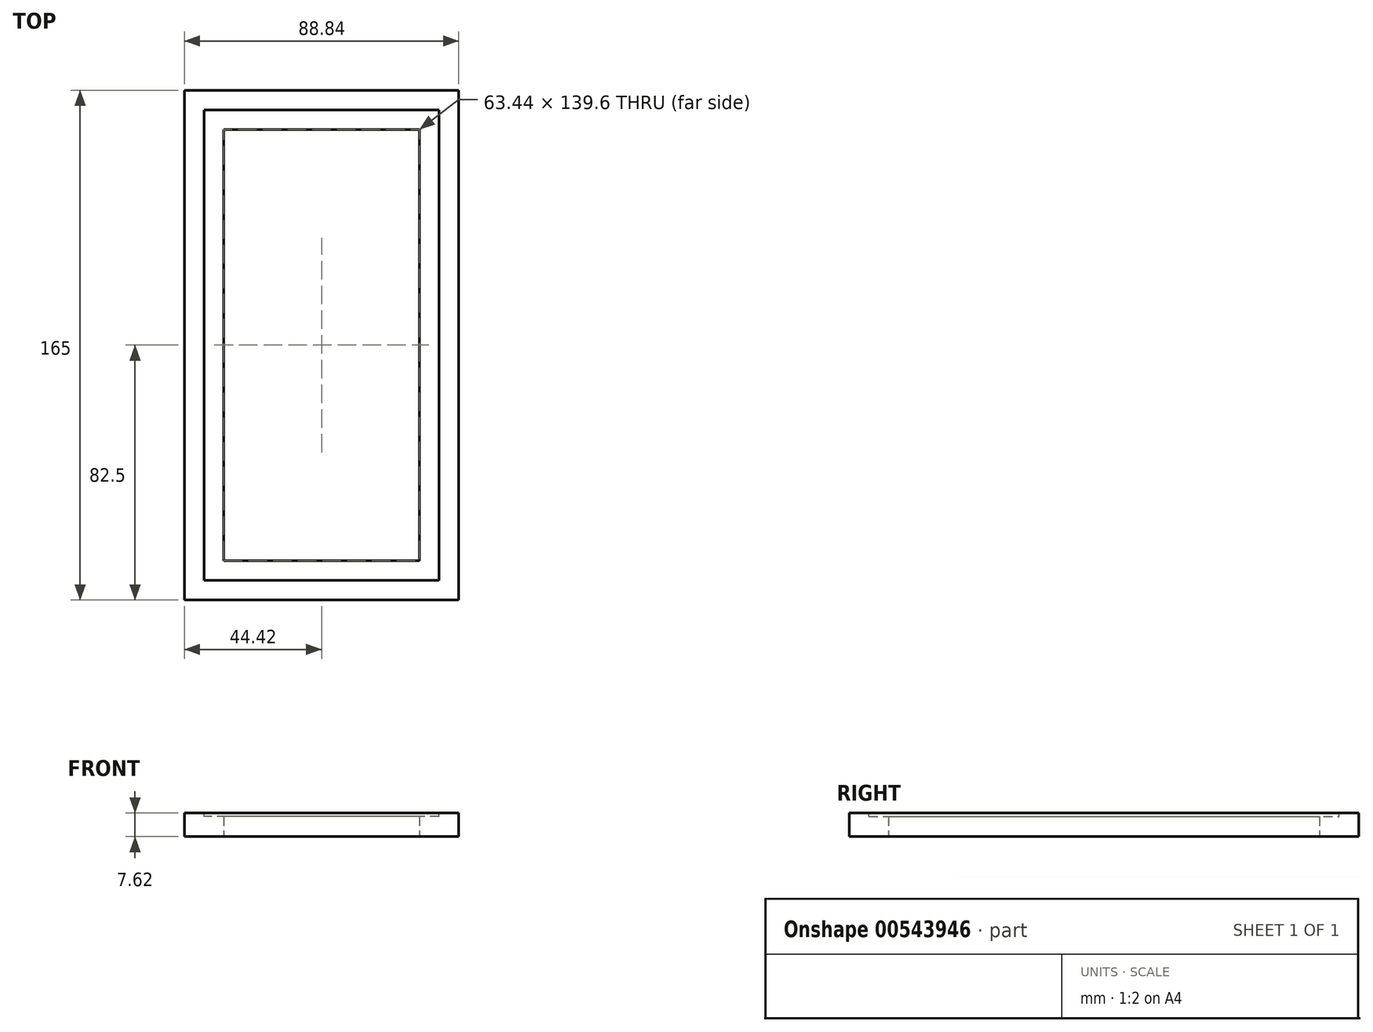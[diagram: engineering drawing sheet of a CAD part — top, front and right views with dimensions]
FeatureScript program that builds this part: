
annotation { "Feature Type Name" : "Feature", "Feature Type Description" : "" }
export const myFeature = defineFeature(function(context is Context, id is Id, definition is map)
    precondition{}
    {
        {
            var Q0;
            Q0=qCreatedBy(makeId("Top.planeOp"),FACE);
            var sketch = newSketch(context, id + "F0", { "sketchPlane" : qUnion([Q0])});
            skLineSegment(sketch, "E0.bottom", {"start": v(44.42, -82.5) * mm, "end": v(-44.42, -82.5) * mm});
            skLineSegment(sketch, "E0.top", {"start": v(44.42, 82.5) * mm, "end": v(-44.42, 82.5) * mm});
            skLineSegment(sketch, "E0.left", {"start": v(44.42, -82.5) * mm, "end": v(44.42, 82.5) * mm});
            skLineSegment(sketch, "E0.right", {"start": v(-44.42, -82.5) * mm, "end": v(-44.42, 82.5) * mm});
            skPoint(sketch, "E0.middle", {"position": v(0, 0) * mm});
            skLineSegment(sketch, "E1.bottom", {"start": v(38.07, -76.15) * mm, "end": v(-38.07, -76.15) * mm});
            skLineSegment(sketch, "E1.top", {"start": v(38.07, 76.15) * mm, "end": v(-38.07, 76.15) * mm});
            skLineSegment(sketch, "E1.left", {"start": v(38.07, -76.15) * mm, "end": v(38.07, 76.15) * mm});
            skLineSegment(sketch, "E1.right", {"start": v(-38.07, -76.15) * mm, "end": v(-38.07, 76.15) * mm});
            skLineSegment(sketch, "E2.bottom", {"start": v(31.72, -69.8) * mm, "end": v(-31.72, -69.8) * mm});
            skLineSegment(sketch, "E2.top", {"start": v(31.72, 69.8) * mm, "end": v(-31.72, 69.8) * mm});
            skLineSegment(sketch, "E2.left", {"start": v(31.72, -69.8) * mm, "end": v(31.72, 69.8) * mm});
            skLineSegment(sketch, "E2.right", {"start": v(-31.72, -69.8) * mm, "end": v(-31.72, 69.8) * mm});
            skSolve(sketch);
        }
        {
            var Q0;
            Q0=makeQuery(id+"F0.imprint","IMPRINT",FACE,{"disambiguationData":[TD([[makeQuery(id+"F0.imprint","IMPRINT",EDGE,{"derivedFrom":sQuery(id+"F0.wireOp",EDGE,"E1.bottom")}),-1.0]])]});
            var Q1;
            Q1=makeQuery(id+"F0.imprint","IMPRINT",FACE,{"disambiguationData":[TD([[makeQuery(id+"F0.imprint","IMPRINT",EDGE,{"derivedFrom":sQuery(id+"F0.wireOp",EDGE,"E0.bottom")}),-1.0]])]});
            extrude(context, id + "F1", {"entities" : qUnion([Q0, Q1]), "depth" : 7.62 * mm, "offsetDistance" : 25.4 * mm});
        }
        {
            var Q0;
            Q0=makeQuery(id+"F1.opExtrude","CAP_FACE",FACE,{"disambiguationData":[OSD([sQuery(id+"F0.wireOp",EDGE,"E0.bottom"),sQuery(id+"F0.wireOp",EDGE,"E0.top"),sQuery(id+"F0.wireOp",EDGE,"E0.left"),sQuery(id+"F0.wireOp",EDGE,"E0.right"),sQuery(id+"F0.wireOp",EDGE,"E1.bottom"),sQuery(id+"F0.wireOp",EDGE,"E1.top"),sQuery(id+"F0.wireOp",EDGE,"E1.left"),sQuery(id+"F0.wireOp",EDGE,"E1.right")])],"isStart":false});
            var sketch = newSketch(context, id + "F2", { "sketchPlane" : qUnion([Q0])});
            skLineSegment(sketch, "E3.bottom", {"start": v(38.07, -76.15) * mm, "end": v(-38.07, -76.15) * mm});
            skLineSegment(sketch, "E3.top", {"start": v(38.07, 76.15) * mm, "end": v(-38.07, 76.15) * mm});
            skLineSegment(sketch, "E3.left", {"start": v(38.07, -76.15) * mm, "end": v(38.07, 76.15) * mm});
            skLineSegment(sketch, "E3.right", {"start": v(-38.07, -76.15) * mm, "end": v(-38.07, 76.15) * mm});
            skPoint(sketch, "E3.middle", {"position": v(0, 0) * mm});
            skSolve(sketch);
        }
        {
            var Q0;
            Q0 = qSketchRegion(id + "F2", true);
            extrude(context, id + "F3", {"entities" : qUnion([Q0]), "operationType" : NewBodyOperationType.REMOVE, "oppositeDirection" : true, "depth" : 1.1 * mm, "offsetDistance" : 25.4 * mm});
        }
    });
